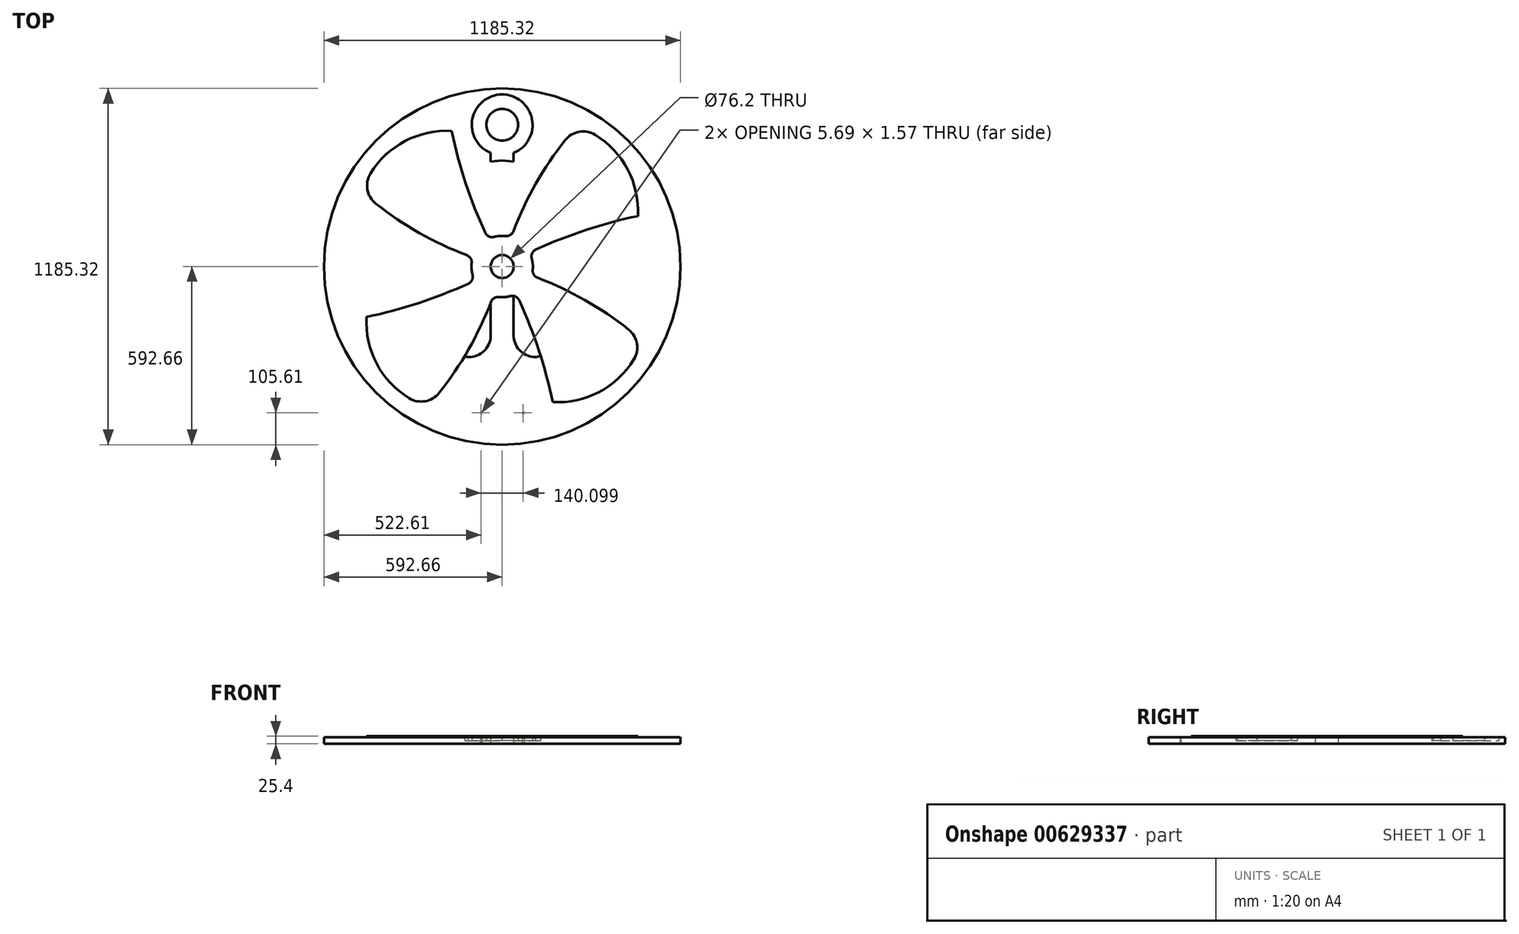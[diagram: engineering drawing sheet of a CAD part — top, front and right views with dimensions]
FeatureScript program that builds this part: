
annotation { "Feature Type Name" : "Feature", "Feature Type Description" : "" }
export const myFeature = defineFeature(function(context is Context, id is Id, definition is map)
    precondition{}
    {
        {
            var Q0;
            Q0=qCreatedBy(makeId("Top.planeOp"),FACE);
            var sketch = newSketch(context, id + "F0", { "sketchPlane" : qUnion([Q0])});
            skCircle(sketch, "E0", {"center": v(0, 471.5) * mm, "radius": 52.78 * mm});
            skLineSegment(sketch, "E1", {"start": v(-38.1, 378.03) * mm, "end": v(-38.1, 348.78) * mm});
            skLineSegment(sketch, "E2", {"start": v(38.1, 378.03) * mm, "end": v(38.1, 348.78) * mm});
            skArc(sketch, "E3", {"start": v(-168.06, 451.17) * mm, "mid": v(-322.67, 417.34) * mm, "end": v(-438.15, 309.1) * mm});
            skArc(sketch, "E4", {"start": v(-420.5, 209.64) * mm, "mid": v(-275.7, 111.94) * mm, "end": v(-117.67, 37.54) * mm});
            skArc(sketch, "E5", {"start": v(-168.06, 451.17) * mm, "mid": v(-121.72, 278.7) * mm, "end": v(-56.67, 112.4) * mm});
            skArc(sketch, "E6", {"start": v(-438.15, 309.1) * mm, "mid": v(-448.17, 256.03) * mm, "end": v(-420.5, 209.64) * mm});
            skArc(sketch, "E7", {"start": v(-451.17, -168.06) * mm, "mid": v(-417.34, -322.67) * mm, "end": v(-309.1, -438.15) * mm});
            skArc(sketch, "E8", {"start": v(-209.64, -420.5) * mm, "mid": v(-111.94, -275.7) * mm, "end": v(-37.54, -117.67) * mm});
            skArc(sketch, "E9", {"start": v(-451.17, -168.06) * mm, "mid": v(-278.7, -121.72) * mm, "end": v(-112.4, -56.67) * mm});
            skArc(sketch, "E10", {"start": v(-309.1, -438.15) * mm, "mid": v(-256.03, -448.17) * mm, "end": v(-209.64, -420.5) * mm});
            skArc(sketch, "E11", {"start": v(168.06, -451.17) * mm, "mid": v(322.67, -417.34) * mm, "end": v(438.15, -309.1) * mm});
            skArc(sketch, "E12", {"start": v(420.5, -209.64) * mm, "mid": v(275.7, -111.94) * mm, "end": v(117.67, -37.54) * mm});
            skArc(sketch, "E13", {"start": v(168.06, -451.17) * mm, "mid": v(121.72, -278.7) * mm, "end": v(56.67, -112.4) * mm});
            skArc(sketch, "E14", {"start": v(438.15, -309.1) * mm, "mid": v(448.17, -256.03) * mm, "end": v(420.5, -209.64) * mm});
            skArc(sketch, "E15", {"start": v(451.17, 168.06) * mm, "mid": v(417.34, 322.67) * mm, "end": v(309.1, 438.15) * mm});
            skArc(sketch, "E16", {"start": v(209.64, 420.5) * mm, "mid": v(111.94, 275.7) * mm, "end": v(37.54, 117.67) * mm});
            skArc(sketch, "E17", {"start": v(451.17, 168.06) * mm, "mid": v(278.7, 121.72) * mm, "end": v(112.4, 56.67) * mm});
            skArc(sketch, "E18", {"start": v(309.1, 438.15) * mm, "mid": v(256.03, 448.17) * mm, "end": v(209.64, 420.5) * mm});
            skArc(sketch, "E19", {"start": v(-101.45, 11.05) * mm, "mid": v(-105.04, 27.07) * mm, "end": v(-117.67, 37.54) * mm});
            skArc(sketch, "E20", {"start": v(-56.67, 112.4) * mm, "mid": v(-44.34, 99.95) * mm, "end": v(-26.87, 98.44) * mm});
            skArc(sketch, "E21", {"start": v(-112.4, -56.67) * mm, "mid": v(-99.95, -44.34) * mm, "end": v(-98.44, -26.87) * mm});
            skArc(sketch, "E22", {"start": v(-11.05, -101.45) * mm, "mid": v(-27.07, -105.04) * mm, "end": v(-37.54, -117.67) * mm});
            skArc(sketch, "E23", {"start": v(56.67, -112.4) * mm, "mid": v(44.34, -99.95) * mm, "end": v(26.87, -98.44) * mm});
            skArc(sketch, "E24", {"start": v(101.45, -11.05) * mm, "mid": v(105.04, -27.07) * mm, "end": v(117.67, -37.54) * mm});
            skArc(sketch, "E25", {"start": v(112.4, 56.67) * mm, "mid": v(99.95, 44.34) * mm, "end": v(98.44, 26.87) * mm});
            skArc(sketch, "E26", {"start": v(11.05, 101.45) * mm, "mid": v(27.07, 105.04) * mm, "end": v(37.54, 117.67) * mm});
            skArc(sketch, "E27", {"start": v(-464.13, -22.7) * mm, "mid": v(-487.85, -53.3) * mm, "end": v(-507.8, -86.48) * mm});
            skArc(sketch, "E28", {"start": v(0, -553.48) * mm, "mid": v(-27.79, -510.48) * mm, "end": v(-72.9, -486.26) * mm});
            skArc(sketch, "E29", {"start": v(72.9, -486.26) * mm, "mid": v(27.79, -510.48) * mm, "end": v(0, -553.48) * mm});
            skArc(sketch, "E30", {"start": v(38.1, -232.52) * mm, "mid": v(62, -282.24) * mm, "end": v(113.73, -301.45) * mm});
            skArc(sketch, "E31", {"start": v(-113.73, -301.45) * mm, "mid": v(-62, -282.24) * mm, "end": v(-38.1, -232.52) * mm});
            skLineSegment(sketch, "E32", {"start": v(-122.73, 339.47) * mm, "end": v(0, 352.96) * mm});
            skLineSegment(sketch, "E33", {"start": v(-122.73, 339.47) * mm, "end": v(-122.73, 315.61) * mm});
            skLineSegment(sketch, "E34", {"start": v(-122.73, 315.61) * mm, "end": v(0, 302.12) * mm});
            skLineSegment(sketch, "E35", {"start": v(122.73, 339.47) * mm, "end": v(0, 352.96) * mm});
            skLineSegment(sketch, "E36", {"start": v(122.73, 339.47) * mm, "end": v(122.73, 315.61) * mm});
            skLineSegment(sketch, "E37", {"start": v(122.73, 315.61) * mm, "end": v(0, 302.12) * mm});
            skArc(sketch, "E38", {"start": v(-410.85, -22.7) * mm, "mid": v(-385.8, -85.63) * mm, "end": v(-350.69, -143.55) * mm});
            skArc(sketch, "E39", {"start": v(410.85, -22.7) * mm, "mid": v(375.54, -40.46) * mm, "end": v(341.23, -60.07) * mm});
            skArc(sketch, "E40", {"start": v(111.67, -301.48) * mm, "mid": v(119.74, -299.55) * mm, "end": v(127.76, -297.45) * mm});
            skCircle(sketch, "E41", {"center": v(0, 0) * mm, "radius": 38.1 * mm});
            skArc(sketch, "E42", {"start": v(-464.13, -22.7) * mm, "mid": v(-451.64, -94.2) * mm, "end": v(-429.68, -163.39) * mm});
            skArc(sketch, "E43", {"start": v(67.2, -487.84) * mm, "mid": v(118.42, -471.23) * mm, "end": v(167.73, -449.61) * mm});
            skArc(sketch, "E44", {"start": v(-433.38, 152.96) * mm, "mid": v(-502.87, 43.27) * mm, "end": v(-507.8, -86.48) * mm});
            skArc(sketch, "E45", {"start": v(507.8, -86.48) * mm, "mid": v(487.85, -53.3) * mm, "end": v(464.13, -22.7) * mm});
            skArc(sketch, "E46", {"start": v(507.8, -86.48) * mm, "mid": v(502.87, 43.27) * mm, "end": v(433.38, 152.96) * mm});
            skArc(sketch, "E47", {"start": v(341.23, -60.07) * mm, "mid": v(393.84, 43.61) * mm, "end": v(433.38, 152.96) * mm});
            skArc(sketch, "E48", {"start": v(-341.23, -60.07) * mm, "mid": v(-375.54, -40.46) * mm, "end": v(-410.85, -22.7) * mm});
            skArc(sketch, "E49", {"start": v(-433.38, 152.96) * mm, "mid": v(-393.84, 43.61) * mm, "end": v(-341.23, -60.07) * mm});
            skArc(sketch, "E50", {"start": v(38.1, 378.03) * mm, "mid": v(0, 572.44) * mm, "end": v(-38.1, 378.03) * mm});
            skLineSegment(sketch, "E51", {"start": v(38.1, -97.96) * mm, "end": v(38.1, -232.52) * mm});
            skLineSegment(sketch, "E52", {"start": v(-38.1, 306.3) * mm, "end": v(-38.1, 97.96) * mm});
            skLineSegment(sketch, "E53", {"start": v(-38.1, -119.14) * mm, "end": v(-38.1, -232.52) * mm});
            skLineSegment(sketch, "E54", {"start": v(38.1, 119.14) * mm, "end": v(38.1, 306.3) * mm});
            skArc(sketch, "E55", {"start": v(11.05, 101.45) * mm, "mid": v(-8.05, 101.73) * mm, "end": v(-26.87, 98.44) * mm});
            skArc(sketch, "E56", {"start": v(-101.45, 11.05) * mm, "mid": v(-101.73, -8.05) * mm, "end": v(-98.44, -26.87) * mm});
            skArc(sketch, "E57", {"start": v(-11.05, -101.45) * mm, "mid": v(8.05, -101.73) * mm, "end": v(26.87, -98.44) * mm});
            skArc(sketch, "E58", {"start": v(101.45, -11.05) * mm, "mid": v(101.73, 8.05) * mm, "end": v(98.44, 26.87) * mm});
            skArc(sketch, "E59", {"start": v(-125.05, -298.18) * mm, "mid": v(-118.37, -299.89) * mm, "end": v(-111.67, -301.48) * mm});
            skArc(sketch, "E60", {"start": v(-212.88, -424.31) * mm, "mid": v(-142.39, -461.45) * mm, "end": v(-67.2, -487.84) * mm});
            skArc(sketch, "E61", {"start": v(343.24, -153.5) * mm, "mid": v(383, -91.17) * mm, "end": v(410.85, -22.7) * mm});
            skArc(sketch, "E62", {"start": v(412.2, -203.12) * mm, "mid": v(446.05, -115.18) * mm, "end": v(464.13, -22.7) * mm});
            skCircle(sketch, "E63", {"center": v(0, 0) * mm, "radius": 592.66 * mm});
            skSolve(sketch);
        }
        {
            var Q0;
            Q0=makeQuery(id+"F0.imprint","IMPRINT",FACE,{"disambiguationData":[TD([[makeQuery(id+"F0.imprint","IMPRINT",EDGE,{"derivedFrom":sQuery(id+"F0.wireOp",EDGE,"E3")}),1.0]])]});
            extrude(context, id + "F1", {"entities" : qUnion([Q0]), "depth" : 25.4 * mm, "offsetDistance" : 25.4 * mm});
        }
        {
            var Q0;
            {var subQ8=sQuery(id+"F0.wireOp",EDGE,"E22");Q0=makeQuery(id+"F0.imprint","IMPRINT",FACE,{"disambiguationData":[TD([[makeQuery(id+"F0.imprint","IMPRINT",EDGE,{"derivedFrom":subQ8}),1.0]])]});}
            var Q1;
            Q1=makeQuery(id+"F0.imprint","IMPRINT",FACE,{"disambiguationData":[TD([[makeQuery(id+"F0.imprint","IMPRINT",EDGE,{"derivedFrom":sQuery(id+"F0.wireOp",EDGE,"E39")}),-1.0]])]});
            var Q2;
            {var subQ4=sQuery(id+"F0.wireOp",EDGE,"E26");Q2=makeQuery(id+"F0.imprint","IMPRINT",FACE,{"disambiguationData":[TD([[makeQuery(id+"F0.imprint","IMPRINT",EDGE,{"derivedFrom":subQ4}),1.0]])]});}
            var Q3;
            {var subQ1=sQuery(id+"F0.wireOp",EDGE,"E33");Q3=makeQuery(id+"F0.imprint","IMPRINT",FACE,{"disambiguationData":[TD([[makeQuery(id+"F0.imprint","IMPRINT",EDGE,{"derivedFrom":subQ1}),1.0]])]});}
            var Q4;
            Q4=makeQuery(id+"F0.imprint","IMPRINT",FACE,{"disambiguationData":[TD([[makeQuery(id+"F0.imprint","IMPRINT",EDGE,{"derivedFrom":sQuery(id+"F0.wireOp",EDGE,"E0")}),1.0]])]});
            var Q5;
            Q5=makeQuery(id+"F0.imprint","IMPRINT",FACE,{"disambiguationData":[TD([[makeQuery(id+"F0.imprint","IMPRINT",EDGE,{"derivedFrom":sQuery(id+"F0.wireOp",EDGE,"E27")}),-1.0]])]});
            extrude(context, id + "F2", {"entities" : qUnion([Q0, Q1, Q2, Q3, Q4, Q5]), "operationType" : NewBodyOperationType.ADD, "depth" : 22 * mm, "offsetDistance" : 25 * mm});
        }
        {
            var Q0;
            {var subQ6=sQuery(id+"F0.wireOp",EDGE,"E1");Q0=makeQuery(id+"F0.imprint","IMPRINT",FACE,{"disambiguationData":[TD([[makeQuery(id+"F0.imprint","IMPRINT",EDGE,{"derivedFrom":subQ6}),-1.0]])]});}
            var Q1;
            {var subQ0=sQuery(id+"F0.wireOp",EDGE,"E40");Q1=makeQuery(id+"F0.imprint","IMPRINT",FACE,{"disambiguationData":[TD([[makeQuery(id+"F0.imprint","IMPRINT",EDGE,{"derivedFrom":subQ0}),1.0]])]});}
            var Q2;
            {var subQ0=sQuery(id+"F0.wireOp",EDGE,"E53");Q2=makeQuery(id+"F0.imprint","IMPRINT",FACE,{"disambiguationData":[TD([[makeQuery(id+"F0.imprint","IMPRINT",EDGE,{"derivedFrom":subQ0}),-1.0]])]});}
            var Q3;
            Q3=makeQuery(id+"F0.imprint","IMPRINT",FACE,{"disambiguationData":[TD([[makeQuery(id+"F0.imprint","IMPRINT",EDGE,{"derivedFrom":sQuery(id+"F0.wireOp",EDGE,"E0")}),-1.0]])]});
            var Q4;
            Q4=makeQuery(id+"F0.imprint","IMPRINT",FACE,{"disambiguationData":[TD([[makeQuery(id+"F0.imprint","IMPRINT",EDGE,{"derivedFrom":sQuery(id+"F0.wireOp",EDGE,"E41")}),-1.0]])]});
            extrude(context, id + "F3", {"entities" : qUnion([Q0, Q1, Q2, Q3, Q4]), "operationType" : NewBodyOperationType.ADD, "depth" : 10 * mm, "offsetDistance" : 25 * mm});
        }
    });
